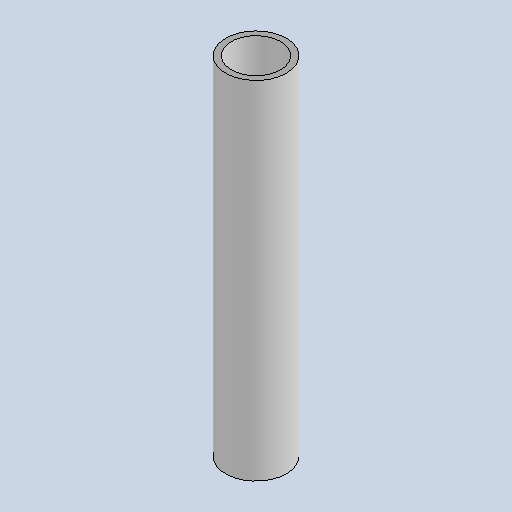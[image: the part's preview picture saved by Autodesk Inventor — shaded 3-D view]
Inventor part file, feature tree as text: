
AUTODESK INVENTOR PART (.ipt)
format: ipt  version: 2025.1 (Build 291241020, 241B)  size: 120,320 bytes
history: native  units: mm
features: extrude x1, sketch x1
ambient origin geometry x8: Origin, YZ Plane, XZ Plane, XY Plane, X Axis, Y Axis, Z Axis, Center Point
bodies: Body1 (feature_tree)
feature tree (2):
  extrude  "Extrusion5"  Depth=120.0mm
  sketch  "Sketch11"  dims[d187=21.0mm d188=2.0mm d189=120.0mm d190=0.0mm]
